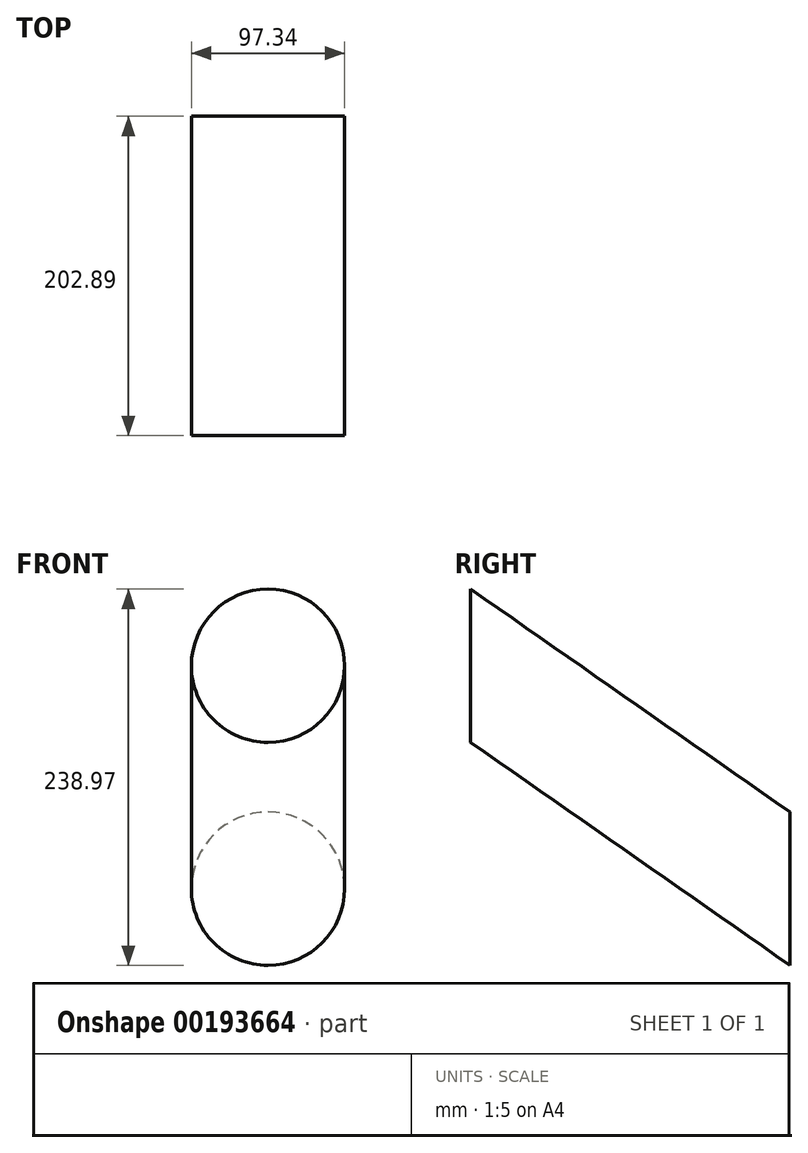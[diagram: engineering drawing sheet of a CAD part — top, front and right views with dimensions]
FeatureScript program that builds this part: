
annotation { "Feature Type Name" : "Feature", "Feature Type Description" : "" }
export const myFeature = defineFeature(function(context is Context, id is Id, definition is map)
    precondition{}
    {
        {
            var Q0;
            Q0=qCreatedBy(makeId("Front.planeOp"),FACE);
            var sketch = newSketch(context, id + "F0", { "sketchPlane" : qUnion([Q0])});
            skCircle(sketch, "E0", {"center": v(0, 0) * mm, "radius": 48.67 * mm});
            skSolve(sketch);
        }
        {
            var Q0;
            Q0=qCreatedBy(makeId("Right.planeOp"),FACE);
            var sketch = newSketch(context, id + "F1", { "sketchPlane" : qUnion([Q0])});
            skLineSegment(sketch, "E1", {"start": v(0, 0) * mm, "end": v(-202.89, 141.63) * mm});
            skSolve(sketch);
        }
        {
            var Q0;
            Q0=makeQuery(id+"F0.imprint","IMPRINT",FACE,{"disambiguationData":[TD([[makeQuery(id+"F0.imprint","IMPRINT",EDGE,{"derivedFrom":sQuery(id+"F0.wireOp",EDGE,"E0")}),1.0]])]});
            var Q1;
            Q1=sQuery(id+"F1.wireOp",EDGE,"E1");
            sweep(context, id + "F2", {"profiles" : qUnion([Q0]), "path" : qUnion([Q1])});
        }
    });
